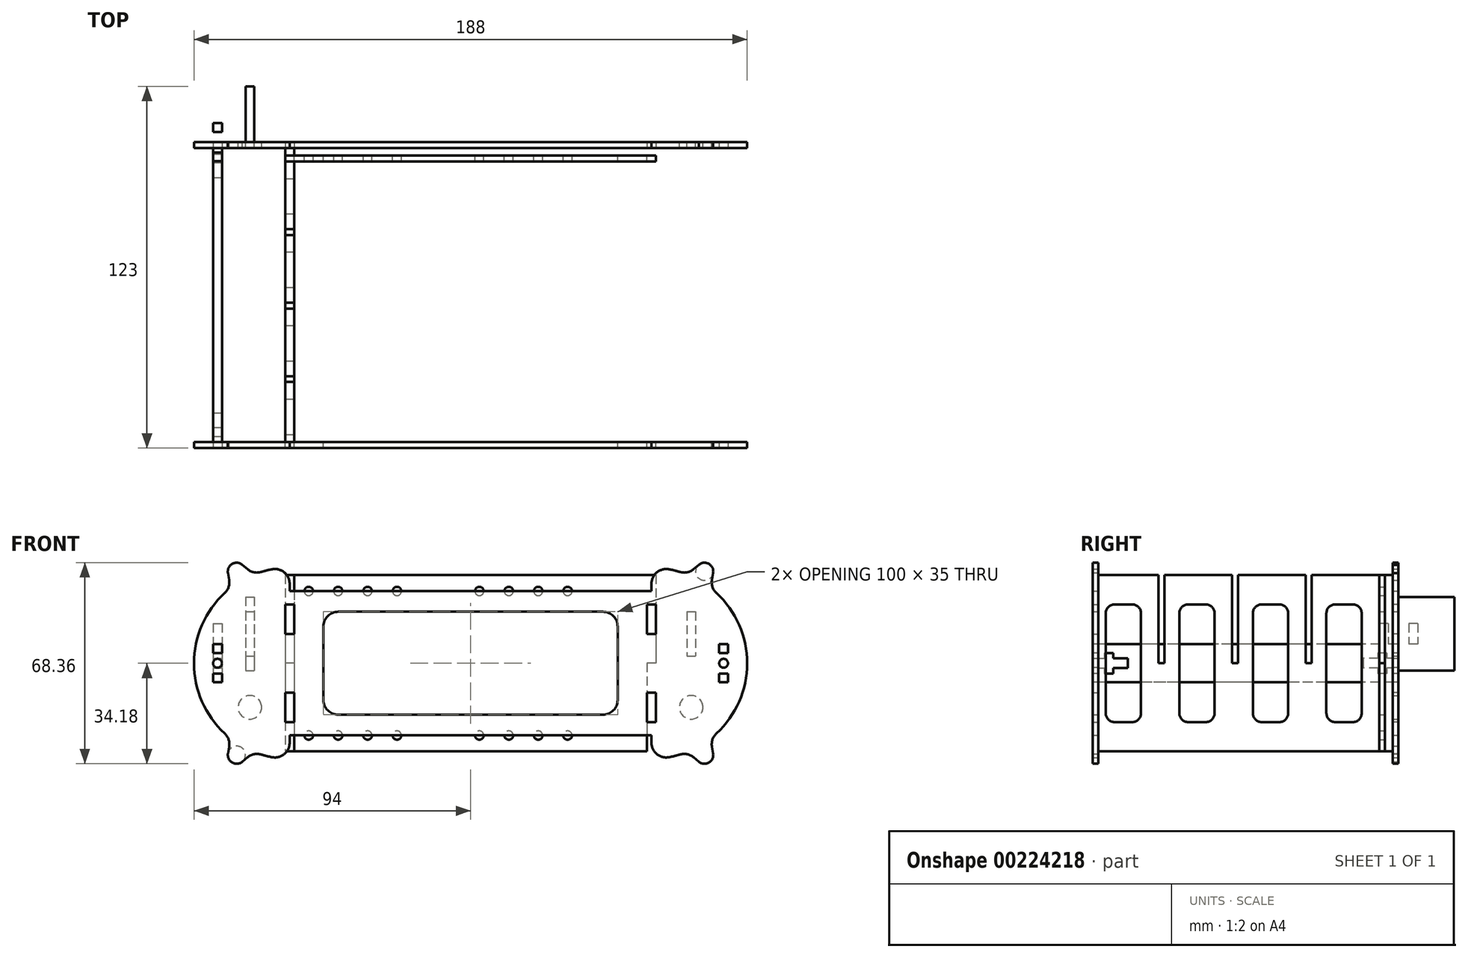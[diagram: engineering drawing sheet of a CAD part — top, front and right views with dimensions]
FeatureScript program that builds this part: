
annotation { "Feature Type Name" : "Feature", "Feature Type Description" : "" }
export const myFeature = defineFeature(function(context is Context, id is Id, definition is map)
    precondition{}
    {
        {
            var Q0;
            Q0=qCreatedBy(makeId("Front.planeOp"),FACE);
            var sketch = newSketch(context, id + "F0", { "sketchPlane" : qUnion([Q0])});
            skLineSegment(sketch, "E0.bottom", {"start": v(-61.5, 42.5) * mm, "end": v(61.5, 42.5) * mm, "construction": true});
            skLineSegment(sketch, "E0.top", {"start": v(-61.5, -42.5) * mm, "end": v(61.5, -42.5) * mm, "construction": true});
            skPoint(sketch, "E0.middle", {"position": v(0, 0) * mm});
            skArc(sketch, "E1", {"start": v(-61.5, 42.5) * mm, "mid": v(-104, 0) * mm, "end": v(-61.5, -42.5) * mm, "construction": true});
            skArc(sketch, "E2", {"start": v(61.5, -42.5) * mm, "mid": v(104, 0) * mm, "end": v(61.5, 42.5) * mm, "construction": true});
            skLineSegment(sketch, "E3.0", {"start": v(-61.5, 39.5) * mm, "end": v(61.5, 39.5) * mm, "construction": true});
            skArc(sketch, "E3.1", {"start": v(-61.5, 39.5) * mm, "mid": v(-101, 0) * mm, "end": v(-61.5, -39.5) * mm, "construction": true});
            skLineSegment(sketch, "E3.2", {"start": v(-61.5, -39.5) * mm, "end": v(61.5, -39.5) * mm, "construction": true});
            skArc(sketch, "E3.3", {"start": v(61.5, -39.5) * mm, "mid": v(101, 0) * mm, "end": v(61.5, 39.5) * mm, "construction": true});
            skArc(sketch, "E4.0", {"start": v(-61.5, 32.5) * mm, "mid": v(-94, 0) * mm, "end": v(-61.5, -32.5) * mm});
            skLineSegment(sketch, "E4.1", {"start": v(-61.5, 32.5) * mm, "end": v(61.5, 32.5) * mm});
            skArc(sketch, "E4.2", {"start": v(61.5, -32.5) * mm, "mid": v(94, 0) * mm, "end": v(61.5, 32.5) * mm});
            skLineSegment(sketch, "E4.3", {"start": v(-61.5, -32.5) * mm, "end": v(61.5, -32.5) * mm});
            skCircle(sketch, "E5", {"center": v(-79.5, 31.18) * mm, "radius": 3 * mm});
            skLineSegment(sketch, "E6", {"start": v(-79.5, 31.18) * mm, "end": v(-61.5, 0) * mm, "construction": true});
            skLineSegment(sketch, "E7", {"start": v(-61.5, 0) * mm, "end": v(-61.5, 32.5) * mm, "construction": true});
            skLineSegment(sketch, "E8", {"start": v(-82.45, 30.66) * mm, "end": v(-81.56, 25.57) * mm});
            skLineSegment(sketch, "E9", {"start": v(-77.57, 33.48) * mm, "end": v(-73.62, 30.16) * mm});
            skLineSegment(sketch, "E10", {"start": v(0, 28.55) * mm, "end": v(0, 0) * mm, "construction": true});
            skLineSegment(sketch, "E11", {"start": v(0, 0) * mm, "end": v(27.55, 0) * mm, "construction": true});
            skCircle(sketch, "E12.MirrorC", {"center": v(79.5, 31.18) * mm, "radius": 3 * mm});
            skLineSegment(sketch, "E13.MirrorCS", {"start": v(77.57, 33.48) * mm, "end": v(73.62, 30.16) * mm});
            skLineSegment(sketch, "E14.MirrorCS", {"start": v(82.45, 30.66) * mm, "end": v(81.56, 25.57) * mm});
            skLineSegment(sketch, "E15.MirrorCS", {"start": v(82.45, -30.66) * mm, "end": v(81.56, -25.57) * mm});
            skCircle(sketch, "E16.MirrorC", {"center": v(79.5, -31.18) * mm, "radius": 3 * mm});
            skLineSegment(sketch, "E17.MirrorCS", {"start": v(77.57, -33.48) * mm, "end": v(73.62, -30.16) * mm});
            skLineSegment(sketch, "E18.MirrorCS", {"start": v(-82.45, -30.66) * mm, "end": v(-81.56, -25.57) * mm});
            skCircle(sketch, "E19.MirrorC", {"center": v(-79.5, -31.18) * mm, "radius": 3 * mm});
            skLineSegment(sketch, "E20.MirrorCS", {"start": v(-77.57, -33.48) * mm, "end": v(-73.62, -30.16) * mm});
            skCircle(sketch, "E21", {"center": v(-75, -15) * mm, "radius": 4 * mm});
            skCircle(sketch, "E22.MirrorC", {"center": v(75, -15) * mm, "radius": 4 * mm});
            skLineSegment(sketch, "E23", {"start": v(-61.5, 32.5) * mm, "end": v(-61.5, 24.5) * mm});
            skLineSegment(sketch, "E24", {"start": v(-61.5, 24.5) * mm, "end": v(61.5, 24.5) * mm});
            skLineSegment(sketch, "E25", {"start": v(61.5, 24.5) * mm, "end": v(61.5, 32.5) * mm});
            skLineSegment(sketch, "E26.MirrorCS", {"start": v(61.5, -24.5) * mm, "end": v(61.5, -32.5) * mm});
            skLineSegment(sketch, "E27.MirrorCS", {"start": v(-61.5, -24.5) * mm, "end": v(61.5, -24.5) * mm});
            skLineSegment(sketch, "E28.MirrorCS", {"start": v(-61.5, 0) * mm, "end": v(-61.5, -32.5) * mm, "construction": true});
            skLineSegment(sketch, "E29", {"start": v(-61.5, -24.5) * mm, "end": v(-61.5, -32.5) * mm});
            skLineSegment(sketch, "E30.bottom", {"start": v(-73.5, 17.5) * mm, "end": v(-76.5, 17.5) * mm});
            skLineSegment(sketch, "E30.top", {"start": v(-73.5, 2.5) * mm, "end": v(-76.5, 2.5) * mm});
            skLineSegment(sketch, "E30.left", {"start": v(-73.5, 17.5) * mm, "end": v(-73.5, 2.5) * mm});
            skLineSegment(sketch, "E30.right", {"start": v(-76.5, 17.5) * mm, "end": v(-76.5, 2.5) * mm});
            skPoint(sketch, "E30.middle", {"position": v(-75, 10) * mm});
            skLineSegment(sketch, "E31.MirrorCS", {"start": v(73.5, 17.5) * mm, "end": v(73.5, 2.5) * mm});
            skLineSegment(sketch, "E32.MirrorCS", {"start": v(73.5, 17.5) * mm, "end": v(76.5, 17.5) * mm});
            skLineSegment(sketch, "E33.MirrorCS", {"start": v(76.5, 17.5) * mm, "end": v(76.5, 2.5) * mm});
            skLineSegment(sketch, "E34.MirrorCS", {"start": v(73.5, 2.5) * mm, "end": v(76.5, 2.5) * mm});
            skSolve(sketch);
        }
        {
            var Q0;
            {var subQ0=sQuery(id+"F0.wireOp",EDGE,"E5");var subQ1=makeQuery(id+"F0.imprint","INTERSECT",VERTEX,{"derivedFrom":[subQ0,sQuery(id+"F0.wireOp",EDGE,"E8")]});Q0=makeQuery(id+"F0.imprint","IMPRINT",FACE,{"disambiguationData":[TD([[makeQuery(id+"F0.imprint","IMPRINT",EDGE,{"disambiguationData":[TD([[subQ1,1.0]])],"derivedFrom":subQ0}),1.0]])]});}
            var Q1;
            {var subQ0=sQuery(id+"F0.wireOp",EDGE,"E12.MirrorC");var subQ1=makeQuery(id+"F0.imprint","INTERSECT",VERTEX,{"derivedFrom":[subQ0,sQuery(id+"F0.wireOp",EDGE,"E13.MirrorCS")]});Q1=makeQuery(id+"F0.imprint","IMPRINT",FACE,{"disambiguationData":[TD([[makeQuery(id+"F0.imprint","IMPRINT",EDGE,{"disambiguationData":[TD([[subQ1,-1.0]])],"derivedFrom":subQ0}),-1.0]])]});}
            var Q2;
            {var subQ0=sQuery(id+"F0.wireOp",EDGE,"E16.MirrorC");var subQ1=makeQuery(id+"F0.imprint","INTERSECT",VERTEX,{"derivedFrom":[sQuery(id+"F0.wireOp",EDGE,"E15.MirrorCS"),subQ0]});Q2=makeQuery(id+"F0.imprint","IMPRINT",FACE,{"disambiguationData":[TD([[makeQuery(id+"F0.imprint","IMPRINT",EDGE,{"disambiguationData":[TD([[subQ1,1.0]])],"derivedFrom":subQ0}),1.0]])]});}
            var Q3;
            {var subQ0=sQuery(id+"F0.wireOp",EDGE,"E19.MirrorC");var subQ1=makeQuery(id+"F0.imprint","INTERSECT",VERTEX,{"derivedFrom":[sQuery(id+"F0.wireOp",EDGE,"E18.MirrorCS"),subQ0]});Q3=makeQuery(id+"F0.imprint","IMPRINT",FACE,{"disambiguationData":[TD([[makeQuery(id+"F0.imprint","IMPRINT",EDGE,{"disambiguationData":[TD([[subQ1,1.0]])],"derivedFrom":subQ0}),-1.0]])]});}
            var Q4;
            {var subQ0=sQuery(id+"F0.wireOp",EDGE,"E8");Q4=makeQuery(id+"F0.imprint","IMPRINT",FACE,{"disambiguationData":[TD([[makeQuery(id+"F0.imprint","IMPRINT",EDGE,{"derivedFrom":subQ0}),1.0]])]});}
            var Q5;
            {var subQ0=sQuery(id+"F0.wireOp",EDGE,"E18.MirrorCS");Q5=makeQuery(id+"F0.imprint","IMPRINT",FACE,{"disambiguationData":[TD([[makeQuery(id+"F0.imprint","IMPRINT",EDGE,{"derivedFrom":subQ0}),-1.0]])]});}
            var Q6;
            {var subQ0=sQuery(id+"F0.wireOp",EDGE,"E15.MirrorCS");Q6=makeQuery(id+"F0.imprint","IMPRINT",FACE,{"disambiguationData":[TD([[makeQuery(id+"F0.imprint","IMPRINT",EDGE,{"derivedFrom":subQ0}),1.0]])]});}
            var Q7;
            {var subQ0=sQuery(id+"F0.wireOp",EDGE,"E13.MirrorCS");Q7=makeQuery(id+"F0.imprint","IMPRINT",FACE,{"disambiguationData":[TD([[makeQuery(id+"F0.imprint","IMPRINT",EDGE,{"derivedFrom":subQ0}),1.0]])]});}
            var Q8;
            Q8=makeQuery(id+"F0.imprint","IMPRINT",FACE,{"disambiguationData":[TD([[makeQuery(id+"F0.imprint","IMPRINT",EDGE,{"derivedFrom":sQuery(id+"F0.wireOp",EDGE,"E21")}),-1.0]])]});
            extrude(context, id + "F1", {"entities" : qUnion([Q0, Q1, Q2, Q3, Q4, Q5, Q6, Q7, Q8]), "depth" : 2 * mm});
        }
        {
            var Q0;
            Q0=makeQuery(id+"F1.opExtrude","SWEPT_EDGE",EDGE,{"disambiguationData":[OSD([sQuery(id+"F0.wireOp",EDGE,"E4.0"),sQuery(id+"F0.wireOp",EDGE,"E9")])]});
            var Q1;
            Q1=makeQuery(id+"F1.opExtrude","SWEPT_EDGE",EDGE,{"disambiguationData":[OSD([sQuery(id+"F0.wireOp",EDGE,"E4.0"),sQuery(id+"F0.wireOp",EDGE,"E8")])]});
            var Q2;
            Q2=makeQuery(id+"F1.opExtrude","SWEPT_EDGE",EDGE,{"disambiguationData":[OSD([sQuery(id+"F0.wireOp",EDGE,"E4.0"),sQuery(id+"F0.wireOp",EDGE,"E4.1"),sQuery(id+"F0.wireOp",EDGE,"E23")])]});
            var Q3;
            Q3=makeQuery(id+"F1.opExtrude","SWEPT_EDGE",EDGE,{"disambiguationData":[OSD([sQuery(id+"F0.wireOp",EDGE,"E4.1"),sQuery(id+"F0.wireOp",EDGE,"E4.2"),sQuery(id+"F0.wireOp",EDGE,"E25")])]});
            var Q4;
            Q4=makeQuery(id+"F1.opExtrude","SWEPT_EDGE",EDGE,{"disambiguationData":[OSD([sQuery(id+"F0.wireOp",EDGE,"E4.2"),sQuery(id+"F0.wireOp",EDGE,"E13.MirrorCS")])]});
            var Q5;
            Q5=makeQuery(id+"F1.opExtrude","SWEPT_EDGE",EDGE,{"disambiguationData":[OSD([sQuery(id+"F0.wireOp",EDGE,"E4.2"),sQuery(id+"F0.wireOp",EDGE,"E14.MirrorCS")])]});
            var Q6;
            Q6=makeQuery(id+"F1.opExtrude","SWEPT_EDGE",EDGE,{"disambiguationData":[OSD([sQuery(id+"F0.wireOp",EDGE,"E4.2"),sQuery(id+"F0.wireOp",EDGE,"E15.MirrorCS")])]});
            var Q7;
            Q7=makeQuery(id+"F1.opExtrude","SWEPT_EDGE",EDGE,{"disambiguationData":[OSD([sQuery(id+"F0.wireOp",EDGE,"E4.2"),sQuery(id+"F0.wireOp",EDGE,"E17.MirrorCS")])]});
            var Q8;
            Q8=makeQuery(id+"F1.opExtrude","SWEPT_EDGE",EDGE,{"disambiguationData":[OSD([sQuery(id+"F0.wireOp",EDGE,"E4.2"),sQuery(id+"F0.wireOp",EDGE,"E4.3"),sQuery(id+"F0.wireOp",EDGE,"E26.MirrorCS")])]});
            var Q9;
            Q9=makeQuery(id+"F1.opExtrude","SWEPT_EDGE",EDGE,{"disambiguationData":[OSD([sQuery(id+"F0.wireOp",EDGE,"E4.0"),sQuery(id+"F0.wireOp",EDGE,"E4.3"),sQuery(id+"F0.wireOp",EDGE,"E29")])]});
            var Q10;
            Q10=makeQuery(id+"F1.opExtrude","SWEPT_EDGE",EDGE,{"disambiguationData":[OSD([sQuery(id+"F0.wireOp",EDGE,"E4.0"),sQuery(id+"F0.wireOp",EDGE,"E20.MirrorCS")])]});
            var Q11;
            Q11=makeQuery(id+"F1.opExtrude","SWEPT_EDGE",EDGE,{"disambiguationData":[OSD([sQuery(id+"F0.wireOp",EDGE,"E4.0"),sQuery(id+"F0.wireOp",EDGE,"E18.MirrorCS")])]});
            fillet(context, id + "F2", {"entities" : qUnion([Q0, Q1, Q2, Q3, Q4, Q5, Q6, Q7, Q8, Q9, Q10, Q11]), "radius" : 5 * mm, "tangentPropagation" : true, "allowEdgeOverflow" : false});
        }
        {
            var Q0;
            Q0=makeQuery(id+"F1.opExtrude","SWEPT_FACE",FACE,{"disambiguationData":[OSD([sQuery(id+"F0.wireOp",EDGE,"E30.left")])]});
            var sketch = newSketch(context, id + "F3", { "sketchPlane" : qUnion([Q0])});
            skPoint(sketch, "E35.0", {"position": v(2, 17.5) * mm});
            skPoint(sketch, "E35.1", {"position": v(0, 2.5) * mm});
            skLineSegment(sketch, "E36.bottom", {"start": v(2, 17.5) * mm, "end": v(0, 17.5) * mm});
            skLineSegment(sketch, "E36.top", {"start": v(2, 2.5) * mm, "end": v(0, 2.5) * mm});
            skLineSegment(sketch, "E36.left", {"start": v(2, 17.5) * mm, "end": v(2, 2.5) * mm});
            skLineSegment(sketch, "E36.right", {"start": v(0, 17.5) * mm, "end": v(0, 2.5) * mm});
            skLineSegment(sketch, "E37.bottom", {"start": v(0, 22.5) * mm, "end": v(-19, 22.5) * mm});
            skLineSegment(sketch, "E37.top", {"start": v(0, -2.5) * mm, "end": v(-19, -2.5) * mm});
            skLineSegment(sketch, "E37.left", {"start": v(0, 22.5) * mm, "end": v(0, -2.5) * mm});
            skLineSegment(sketch, "E37.right", {"start": v(-19, 22.5) * mm, "end": v(-19, -2.5) * mm});
            skPoint(sketch, "E38", {"position": v(0, 10) * mm});
            skSolve(sketch);
        }
        {
            var Q0;
            Q0 = qSketchRegion(id + "F3", true);
            extrude(context, id + "F4", {"entities" : qUnion([Q0]), "depth" : 3 * mm});
        }
        {
            var Q0;
            Q0=makeQuery(id+"F1.opExtrude","CAP_FACE",FACE,{"disambiguationData":[OSD([sQuery(id+"F0.wireOp",EDGE,"E4.0"),sQuery(id+"F0.wireOp",EDGE,"E4.2"),sQuery(id+"F0.wireOp",EDGE,"E5"),sQuery(id+"F0.wireOp",EDGE,"E8"),sQuery(id+"F0.wireOp",EDGE,"E9"),sQuery(id+"F0.wireOp",EDGE,"E12.MirrorC"),sQuery(id+"F0.wireOp",EDGE,"E13.MirrorCS"),sQuery(id+"F0.wireOp",EDGE,"E14.MirrorCS"),sQuery(id+"F0.wireOp",EDGE,"E15.MirrorCS"),sQuery(id+"F0.wireOp",EDGE,"E16.MirrorC"),sQuery(id+"F0.wireOp",EDGE,"E17.MirrorCS"),sQuery(id+"F0.wireOp",EDGE,"E18.MirrorCS"),sQuery(id+"F0.wireOp",EDGE,"E19.MirrorC"),sQuery(id+"F0.wireOp",EDGE,"E20.MirrorCS"),sQuery(id+"F0.wireOp",EDGE,"E21"),sQuery(id+"F0.wireOp",EDGE,"E22.MirrorC"),sQuery(id+"F0.wireOp",EDGE,"E23"),sQuery(id+"F0.wireOp",EDGE,"E24"),sQuery(id+"F0.wireOp",EDGE,"E25"),sQuery(id+"F0.wireOp",EDGE,"E26.MirrorCS"),sQuery(id+"F0.wireOp",EDGE,"E27.MirrorCS"),sQuery(id+"F0.wireOp",EDGE,"E29"),sQuery(id+"F0.wireOp",EDGE,"E30.bottom"),sQuery(id+"F0.wireOp",EDGE,"E30.top"),sQuery(id+"F0.wireOp",EDGE,"E30.left"),sQuery(id+"F0.wireOp",EDGE,"E30.right"),sQuery(id+"F0.wireOp",EDGE,"E31.MirrorCS"),sQuery(id+"F0.wireOp",EDGE,"E32.MirrorCS"),sQuery(id+"F0.wireOp",EDGE,"E33.MirrorCS"),sQuery(id+"F0.wireOp",EDGE,"E34.MirrorCS")])],"isStart":false});
            var sketch = newSketch(context, id + "F5", { "sketchPlane" : qUnion([Q0])});
            skLineSegment(sketch, "E39.bottom", {"start": v(60, 20) * mm, "end": v(63, 20) * mm});
            skLineSegment(sketch, "E39.top", {"start": v(60, 10) * mm, "end": v(63, 10) * mm});
            skLineSegment(sketch, "E39.left", {"start": v(60, 20) * mm, "end": v(60, 10) * mm});
            skLineSegment(sketch, "E39.right", {"start": v(63, 20) * mm, "end": v(63, 10) * mm});
            skLineSegment(sketch, "E40", {"start": v(0, 0) * mm, "end": v(0, 17.53) * mm, "construction": true});
            skLineSegment(sketch, "E41", {"start": v(0, 0) * mm, "end": v(16.07, 0) * mm, "construction": true});
            skLineSegment(sketch, "E42.MirrorCS", {"start": v(60, -20) * mm, "end": v(63, -20) * mm});
            skLineSegment(sketch, "E43.MirrorCS", {"start": v(60, -10) * mm, "end": v(63, -10) * mm});
            skLineSegment(sketch, "E44.MirrorCS", {"start": v(60, -20) * mm, "end": v(60, -10) * mm});
            skLineSegment(sketch, "E45.MirrorCS", {"start": v(63, -20) * mm, "end": v(63, -10) * mm});
            skLineSegment(sketch, "E46.MirrorCS", {"start": v(-60, 10) * mm, "end": v(-63, 10) * mm});
            skLineSegment(sketch, "E47.MirrorCS", {"start": v(-60, 20) * mm, "end": v(-60, 10) * mm});
            skLineSegment(sketch, "E48.MirrorCS", {"start": v(-63, 20) * mm, "end": v(-63, 10) * mm});
            skLineSegment(sketch, "E49.MirrorCS", {"start": v(-60, 20) * mm, "end": v(-63, 20) * mm});
            skLineSegment(sketch, "E50.MirrorCS", {"start": v(-60, -20) * mm, "end": v(-60, -10) * mm});
            skLineSegment(sketch, "E51.MirrorCS", {"start": v(-60, -20) * mm, "end": v(-63, -20) * mm});
            skLineSegment(sketch, "E52.MirrorCS", {"start": v(-63, -20) * mm, "end": v(-63, -10) * mm});
            skLineSegment(sketch, "E53.MirrorCS", {"start": v(-60, -10) * mm, "end": v(-63, -10) * mm});
            skSolve(sketch);
        }
        {
            var Q0;
            Q0 = qSketchRegion(id + "F5", true);
            extrude(context, id + "F6", {"entities" : qUnion([Q0]), "operationType" : NewBodyOperationType.REMOVE, "oppositeDirection" : true, "depth" : 25 * mm});
        }
        {
            var Q0;
            Q0=makeQuery(id+"F6.boolean.opBoolean","COPY",FACE,{"derivedFrom":makeQuery(id+"F6.opExtrude","SWEPT_FACE",FACE,{"disambiguationData":[OSD([sQuery(id+"F5.wireOp",EDGE,"E48.MirrorCS")])]})});
            var sketch = newSketch(context, id + "F7", { "sketchPlane" : qUnion([Q0])});
            skLineSegment(sketch, "E54.bottom", {"start": v(-2, 30) * mm, "end": v(-102, 30) * mm});
            skLineSegment(sketch, "E54.top", {"start": v(-2, -30) * mm, "end": v(-102, -30) * mm});
            skLineSegment(sketch, "E54.left", {"start": v(-2, 30) * mm, "end": v(-2, -30) * mm});
            skLineSegment(sketch, "E54.right", {"start": v(-102, 30) * mm, "end": v(-102, -30) * mm});
            skPoint(sketch, "E54.middle", {"position": v(-52, 0) * mm});
            skLineSegment(sketch, "E55.0.0", {"start": v(0, 20) * mm, "end": v(-2, 20) * mm});
            skLineSegment(sketch, "E55.0.1", {"start": v(-2, 20) * mm, "end": v(-2, 10) * mm});
            skLineSegment(sketch, "E55.0.2", {"start": v(-2, 10) * mm, "end": v(0, 10) * mm});
            skLineSegment(sketch, "E55.0.3", {"start": v(0, 10) * mm, "end": v(0, 20) * mm});
            skLineSegment(sketch, "E55.1.0", {"start": v(0, -20) * mm, "end": v(0, -10) * mm});
            skLineSegment(sketch, "E55.1.1", {"start": v(0, -10) * mm, "end": v(-2, -10) * mm});
            skLineSegment(sketch, "E55.1.2", {"start": v(-2, -10) * mm, "end": v(-2, -20) * mm});
            skLineSegment(sketch, "E55.1.3", {"start": v(-2, -20) * mm, "end": v(0, -20) * mm});
            skLineSegment(sketch, "E56", {"start": v(-52, 30) * mm, "end": v(-52, -30) * mm, "construction": true});
            skLineSegment(sketch, "E57.MirrorCS", {"start": v(-104, 20) * mm, "end": v(-102, 20) * mm});
            skLineSegment(sketch, "E58.MirrorCS", {"start": v(-104, 10) * mm, "end": v(-104, 20) * mm});
            skLineSegment(sketch, "E59.MirrorCS", {"start": v(-102, 10) * mm, "end": v(-104, 10) * mm});
            skLineSegment(sketch, "E60.MirrorCS", {"start": v(-104, -10) * mm, "end": v(-102, -10) * mm});
            skLineSegment(sketch, "E61.MirrorCS", {"start": v(-104, -20) * mm, "end": v(-104, -10) * mm});
            skLineSegment(sketch, "E62.MirrorCS", {"start": v(-102, -20) * mm, "end": v(-104, -20) * mm});
            skLineSegment(sketch, "E63.bottom", {"start": v(-4.58, 30) * mm, "end": v(-6.58, 30) * mm});
            skLineSegment(sketch, "E63.top", {"start": v(-4.58, 0) * mm, "end": v(-6.58, 0) * mm});
            skLineSegment(sketch, "E63.left", {"start": v(-4.58, 30) * mm, "end": v(-4.58, 0) * mm});
            skLineSegment(sketch, "E63.right", {"start": v(-6.58, 30) * mm, "end": v(-6.58, 0) * mm});
            skPoint(sketch, "E63.middle", {"position": v(-5.58, 15) * mm});
            skLineSegment(sketch, "E64", {"start": v(-52, 0) * mm, "end": v(-39.54, 0) * mm, "construction": true});
            skLineSegment(sketch, "E65.bottom", {"start": v(-15.5, 20) * mm, "end": v(-21.5, 20) * mm});
            skLineSegment(sketch, "E65.top", {"start": v(-15.5, -20) * mm, "end": v(-21.5, -20) * mm});
            skLineSegment(sketch, "E65.left", {"start": v(-12.5, 17) * mm, "end": v(-12.5, -17) * mm});
            skLineSegment(sketch, "E65.right", {"start": v(-24.5, 17) * mm, "end": v(-24.5, -17) * mm});
            skPoint(sketch, "E65.middle", {"position": v(-18.5, 0) * mm});
            skPoint(sketch, "E66", {"position": v(-18.5, 18.1) * mm});
            skPoint(sketch, "E67.visualSharp", {"position": v(-24.5, 20) * mm});
            skArc(sketch, "E67.filletArc", {"start": v(-21.5, 20) * mm, "mid": v(-23.62, 19.12) * mm, "end": v(-24.5, 17) * mm});
            skPoint(sketch, "E68.visualSharp", {"position": v(-12.5, 20) * mm});
            skArc(sketch, "E68.filletArc", {"start": v(-12.5, 17) * mm, "mid": v(-13.38, 19.12) * mm, "end": v(-15.5, 20) * mm});
            skPoint(sketch, "E69.visualSharp", {"position": v(-12.5, -20) * mm});
            skArc(sketch, "E69.filletArc", {"start": v(-15.5, -20) * mm, "mid": v(-13.38, -19.12) * mm, "end": v(-12.5, -17) * mm});
            skPoint(sketch, "E70.visualSharp", {"position": v(-24.5, -20) * mm});
            skArc(sketch, "E70.filletArc", {"start": v(-24.5, -17) * mm, "mid": v(-23.62, -19.12) * mm, "end": v(-21.5, -20) * mm});
            skLineSegment(sketch, "E71.1.0.0", {"start": v(-40.5, 20) * mm, "end": v(-46.5, 20) * mm});
            skArc(sketch, "E71.1.0.1", {"start": v(-46.5, 20) * mm, "mid": v(-48.62, 19.12) * mm, "end": v(-49.5, 17) * mm});
            skArc(sketch, "E71.1.0.2", {"start": v(-37.5, 17) * mm, "mid": v(-38.38, 19.12) * mm, "end": v(-40.5, 20) * mm});
            skLineSegment(sketch, "E71.1.0.3", {"start": v(-37.5, 17) * mm, "end": v(-37.5, -17) * mm});
            skArc(sketch, "E71.1.0.4", {"start": v(-40.5, -20) * mm, "mid": v(-38.38, -19.12) * mm, "end": v(-37.5, -17) * mm});
            skLineSegment(sketch, "E71.1.0.5", {"start": v(-40.5, -20) * mm, "end": v(-46.5, -20) * mm});
            skArc(sketch, "E71.1.0.6", {"start": v(-49.5, -17) * mm, "mid": v(-48.62, -19.12) * mm, "end": v(-46.5, -20) * mm});
            skLineSegment(sketch, "E71.1.0.7", {"start": v(-49.5, 17) * mm, "end": v(-49.5, -17) * mm});
            skLineSegment(sketch, "E71.2.0.0", {"start": v(-65.5, 20) * mm, "end": v(-71.5, 20) * mm});
            skArc(sketch, "E71.2.0.1", {"start": v(-71.5, 20) * mm, "mid": v(-73.62, 19.12) * mm, "end": v(-74.5, 17) * mm});
            skArc(sketch, "E71.2.0.2", {"start": v(-62.5, 17) * mm, "mid": v(-63.38, 19.12) * mm, "end": v(-65.5, 20) * mm});
            skLineSegment(sketch, "E71.2.0.3", {"start": v(-62.5, 17) * mm, "end": v(-62.5, -17) * mm});
            skArc(sketch, "E71.2.0.4", {"start": v(-65.5, -20) * mm, "mid": v(-63.38, -19.12) * mm, "end": v(-62.5, -17) * mm});
            skLineSegment(sketch, "E71.2.0.5", {"start": v(-65.5, -20) * mm, "end": v(-71.5, -20) * mm});
            skArc(sketch, "E71.2.0.6", {"start": v(-74.5, -17) * mm, "mid": v(-73.62, -19.12) * mm, "end": v(-71.5, -20) * mm});
            skLineSegment(sketch, "E71.2.0.7", {"start": v(-74.5, 17) * mm, "end": v(-74.5, -17) * mm});
            skLineSegment(sketch, "E71.direction1", {"start": v(-21.5, 20) * mm, "end": v(-46.5, 20) * mm, "construction": true});
            skLineSegment(sketch, "E72.0.3.0", {"start": v(-90.5, 20) * mm, "end": v(-96.5, 20) * mm});
            skArc(sketch, "E72.3.3.0", {"start": v(-96.5, 20) * mm, "mid": v(-98.62, 19.12) * mm, "end": v(-99.5, 17) * mm});
            skArc(sketch, "E72.7.3.0", {"start": v(-87.5, 17) * mm, "mid": v(-88.38, 19.12) * mm, "end": v(-90.5, 20) * mm});
            skLineSegment(sketch, "E72.11.3.0", {"start": v(-87.5, 17) * mm, "end": v(-87.5, -17) * mm});
            skArc(sketch, "E72.14.3.0", {"start": v(-90.5, -20) * mm, "mid": v(-88.38, -19.12) * mm, "end": v(-87.5, -17) * mm});
            skLineSegment(sketch, "E72.18.3.0", {"start": v(-90.5, -20) * mm, "end": v(-96.5, -20) * mm});
            skArc(sketch, "E72.21.3.0", {"start": v(-99.5, -17) * mm, "mid": v(-98.62, -19.12) * mm, "end": v(-96.5, -20) * mm});
            skLineSegment(sketch, "E72.25.3.0", {"start": v(-99.5, 17) * mm, "end": v(-99.5, -17) * mm});
            skLineSegment(sketch, "E73.0.1.0", {"start": v(-31.58, 30) * mm, "end": v(-31.58, 0) * mm});
            skLineSegment(sketch, "E73.3.1.0", {"start": v(-29.58, 30) * mm, "end": v(-31.58, 30) * mm});
            skLineSegment(sketch, "E73.6.1.0", {"start": v(-29.58, 30) * mm, "end": v(-29.58, 0) * mm});
            skLineSegment(sketch, "E73.9.1.0", {"start": v(-29.58, 0) * mm, "end": v(-31.58, 0) * mm});
            skLineSegment(sketch, "E73.0.2.0", {"start": v(-56.58, 30) * mm, "end": v(-56.58, 0) * mm});
            skLineSegment(sketch, "E73.3.2.0", {"start": v(-54.58, 30) * mm, "end": v(-56.58, 30) * mm});
            skLineSegment(sketch, "E73.6.2.0", {"start": v(-54.58, 30) * mm, "end": v(-54.58, 0) * mm});
            skLineSegment(sketch, "E73.9.2.0", {"start": v(-54.58, 0) * mm, "end": v(-56.58, 0) * mm});
            skLineSegment(sketch, "E73.0.3.0", {"start": v(-81.58, 30) * mm, "end": v(-81.58, 0) * mm});
            skLineSegment(sketch, "E73.3.3.0", {"start": v(-79.58, 30) * mm, "end": v(-81.58, 30) * mm});
            skLineSegment(sketch, "E73.6.3.0", {"start": v(-79.58, 30) * mm, "end": v(-79.58, 0) * mm});
            skLineSegment(sketch, "E73.9.3.0", {"start": v(-79.58, 0) * mm, "end": v(-81.58, 0) * mm});
            skSolve(sketch);
        }
        {
            var Q0;
            {var subQ9=sQuery(id+"F7.wireOp",EDGE,"E54.top");Q0=makeQuery(id+"F7.imprint","IMPRINT",FACE,{"disambiguationData":[TD([[makeQuery(id+"F7.imprint","IMPRINT",EDGE,{"derivedFrom":subQ9}),-1.0]])]});}
            var Q1;
            {var subQ0=sQuery(id+"F7.wireOp",EDGE,"E57.MirrorCS");Q1=makeQuery(id+"F7.imprint","IMPRINT",FACE,{"disambiguationData":[TD([[makeQuery(id+"F7.imprint","IMPRINT",EDGE,{"derivedFrom":subQ0}),-1.0]])]});}
            var Q2;
            {var subQ0=sQuery(id+"F7.wireOp",EDGE,"E60.MirrorCS");Q2=makeQuery(id+"F7.imprint","IMPRINT",FACE,{"disambiguationData":[TD([[makeQuery(id+"F7.imprint","IMPRINT",EDGE,{"derivedFrom":subQ0}),-1.0]])]});}
            var Q3;
            Q3=makeQuery(id+"F7.imprint","IMPRINT",FACE,{"disambiguationData":[TD([[makeQuery(id+"F7.imprint","IMPRINT",EDGE,{"derivedFrom":sQuery(id+"F7.wireOp",EDGE,"E55.0.0")}),1.0]])]});
            var Q4;
            Q4=makeQuery(id+"F7.imprint","IMPRINT",FACE,{"disambiguationData":[TD([[makeQuery(id+"F7.imprint","IMPRINT",EDGE,{"derivedFrom":sQuery(id+"F7.wireOp",EDGE,"E55.1.0")}),1.0]])]});
            extrude(context, id + "F8", {"entities" : qUnion([Q0, Q1, Q2, Q3, Q4]), "depth" : 3 * mm});
        }
        {
            var Q0;
            Q0=makeQuery(id+"F8.opExtrude","SWEPT_FACE",FACE,{"disambiguationData":[OSD([sQuery(id+"F7.wireOp",EDGE,"E63.left")])]});
            var sketch = newSketch(context, id + "F9", { "sketchPlane" : qUnion([Q0])});
            skLineSegment(sketch, "E74.bottom", {"start": v(-60, 30) * mm, "end": v(60, 30) * mm});
            skLineSegment(sketch, "E74.top", {"start": v(-60, -30) * mm, "end": v(60, -30) * mm});
            skLineSegment(sketch, "E74.left", {"start": v(-60, 30) * mm, "end": v(-60, -30) * mm});
            skLineSegment(sketch, "E74.right", {"start": v(60, 30) * mm, "end": v(60, -30) * mm});
            skPoint(sketch, "E74.middle", {"position": v(0, 0) * mm});
            skLineSegment(sketch, "E75", {"start": v(0, 0) * mm, "end": v(0, 15.93) * mm, "construction": true});
            skCircle(sketch, "E76", {"center": v(-55, 24.5) * mm, "radius": 1.5 * mm});
            skCircle(sketch, "E77", {"center": v(3, 24.5) * mm, "radius": 1.5 * mm});
            skCircle(sketch, "E78", {"center": v(-55, -24.5) * mm, "radius": 1.5 * mm});
            skCircle(sketch, "E79", {"center": v(3, -24.5) * mm, "radius": 1.5 * mm});
            skLineSegment(sketch, "E80", {"start": v(3, 24.5) * mm, "end": v(3, -24.5) * mm, "construction": true});
            skPoint(sketch, "E81", {"position": v(3, 0) * mm});
            skCircle(sketch, "E82.1.0.0", {"center": v(-45, 24.5) * mm, "radius": 1.5 * mm});
            skCircle(sketch, "E82.1.0.1", {"center": v(13, 24.5) * mm, "radius": 1.5 * mm});
            skCircle(sketch, "E82.1.0.2", {"center": v(13, -24.5) * mm, "radius": 1.5 * mm});
            skCircle(sketch, "E82.1.0.3", {"center": v(-45, -24.5) * mm, "radius": 1.5 * mm});
            skCircle(sketch, "E82.2.0.0", {"center": v(-35, 24.5) * mm, "radius": 1.5 * mm});
            skCircle(sketch, "E82.2.0.1", {"center": v(23, 24.5) * mm, "radius": 1.5 * mm});
            skCircle(sketch, "E82.2.0.2", {"center": v(23, -24.5) * mm, "radius": 1.5 * mm});
            skCircle(sketch, "E82.2.0.3", {"center": v(-35, -24.5) * mm, "radius": 1.5 * mm});
            skCircle(sketch, "E82.3.0.0", {"center": v(-25, 24.5) * mm, "radius": 1.5 * mm});
            skCircle(sketch, "E82.3.0.1", {"center": v(33, 24.5) * mm, "radius": 1.5 * mm});
            skCircle(sketch, "E82.3.0.2", {"center": v(33, -24.5) * mm, "radius": 1.5 * mm});
            skCircle(sketch, "E82.3.0.3", {"center": v(-25, -24.5) * mm, "radius": 1.5 * mm});
            skLineSegment(sketch, "E82.direction1", {"start": v(-55, 24.5) * mm, "end": v(-45, 24.5) * mm, "construction": true});
            skLineSegment(sketch, "E83.bottom", {"start": v(-45, 17.5) * mm, "end": v(45, 17.5) * mm});
            skLineSegment(sketch, "E83.top", {"start": v(-45, -17.5) * mm, "end": v(45, -17.5) * mm});
            skLineSegment(sketch, "E83.left", {"start": v(-50, 12.5) * mm, "end": v(-50, -12.5) * mm});
            skLineSegment(sketch, "E83.right", {"start": v(50, 12.5) * mm, "end": v(50, -12.5) * mm});
            skPoint(sketch, "E84.visualSharp", {"position": v(-50, 17.5) * mm});
            skArc(sketch, "E84.filletArc", {"start": v(-45, 17.5) * mm, "mid": v(-48.54, 16.04) * mm, "end": v(-50, 12.5) * mm});
            skPoint(sketch, "E85.visualSharp", {"position": v(-50, -17.5) * mm});
            skArc(sketch, "E85.filletArc", {"start": v(-50, -12.5) * mm, "mid": v(-48.54, -16.04) * mm, "end": v(-45, -17.5) * mm});
            skPoint(sketch, "E86.visualSharp", {"position": v(50, -17.5) * mm});
            skArc(sketch, "E86.filletArc", {"start": v(45, -17.5) * mm, "mid": v(48.54, -16.04) * mm, "end": v(50, -12.5) * mm});
            skPoint(sketch, "E87.visualSharp", {"position": v(50, 17.5) * mm});
            skArc(sketch, "E87.filletArc", {"start": v(50, 12.5) * mm, "mid": v(48.54, 16.04) * mm, "end": v(45, 17.5) * mm});
            skLineSegment(sketch, "E88.0.0", {"start": v(-63, 30) * mm, "end": v(-63, 0) * mm});
            skLineSegment(sketch, "E88.0.1", {"start": v(-63, 0) * mm, "end": v(-60, 0) * mm});
            skLineSegment(sketch, "E88.0.2", {"start": v(-60, 0) * mm, "end": v(-60, 30) * mm});
            skLineSegment(sketch, "E88.0.3", {"start": v(-60, 30) * mm, "end": v(-63, 30) * mm});
            skLineSegment(sketch, "E89.MirrorCS", {"start": v(60, 30) * mm, "end": v(63, 30) * mm});
            skLineSegment(sketch, "E90.MirrorCS", {"start": v(63, 30) * mm, "end": v(63, 0) * mm});
            skLineSegment(sketch, "E91.MirrorCS", {"start": v(63, 0) * mm, "end": v(60, 0) * mm});
            skSolve(sketch);
        }
        {
            var Q0;
            Q0 = qSketchRegion(id + "F9", true);
            extrude(context, id + "F10", {"entities" : qUnion([Q0]), "depth" : 2 * mm});
        }
        {
            var Q0;
            {var subQ0=sQuery(id+"F7.wireOp",EDGE,"E54.right");Q0=makeQuery(id+"F8.opExtrude","SWEPT_FACE",FACE,{"disambiguationData":[OSD([subQ0]),TDD([makeQuery(id+"F7.imprint","IMPRINT",EDGE,{"disambiguationData":[TD([[makeQuery(id+"F7.imprint","INTERSECT",VERTEX,{"derivedFrom":[sQuery(id+"F7.wireOp",EDGE,"E54.bottom"),subQ0]}),-1.0]])],"derivedFrom":subQ0})])]});}
            var sketch = newSketch(context, id + "F11", { "sketchPlane" : qUnion([Q0])});
            skLineSegment(sketch, "E92.0.0", {"start": v(-61.5, 24.5) * mm, "end": v(-61.5, 27.04) * mm});
            skArc(sketch, "E92.0.1", {"start": v(-61.5, 27.04) * mm, "mid": v(-63.3, 30.89) * mm, "end": v(-67.4, 31.96) * mm});
            skArc(sketch, "E92.0.2", {"start": v(-67.4, 31.96) * mm, "mid": v(-69.27, 31.56) * mm, "end": v(-71.11, 31.05) * mm});
            skArc(sketch, "E92.0.3", {"start": v(-71.11, 31.05) * mm, "mid": v(-73.58, 30.92) * mm, "end": v(-75.8, 32) * mm});
            skLineSegment(sketch, "E92.0.4", {"start": v(-75.8, 32) * mm, "end": v(-77.57, 33.48) * mm});
            skArc(sketch, "E92.0.5", {"start": v(-77.57, 33.48) * mm, "mid": v(-81, 33.77) * mm, "end": v(-82.45, 30.66) * mm});
            skLineSegment(sketch, "E92.0.6", {"start": v(-82.45, 30.66) * mm, "end": v(-82.05, 28.38) * mm});
            skArc(sketch, "E92.0.7", {"start": v(-82.05, 28.38) * mm, "mid": v(-82.24, 25.92) * mm, "end": v(-83.58, 23.85) * mm});
            skArc(sketch, "E92.0.8", {"start": v(-83.58, 23.85) * mm, "mid": v(-94, 0) * mm, "end": v(-83.58, -23.85) * mm});
            skArc(sketch, "E92.0.9", {"start": v(-83.58, -23.85) * mm, "mid": v(-82.24, -25.92) * mm, "end": v(-82.05, -28.38) * mm});
            skLineSegment(sketch, "E92.0.10", {"start": v(-82.05, -28.38) * mm, "end": v(-82.45, -30.66) * mm});
            skArc(sketch, "E92.0.11", {"start": v(-82.45, -30.66) * mm, "mid": v(-81, -33.77) * mm, "end": v(-77.57, -33.48) * mm});
            skLineSegment(sketch, "E92.0.12", {"start": v(-77.57, -33.48) * mm, "end": v(-75.8, -32) * mm});
            skArc(sketch, "E92.0.13", {"start": v(-75.8, -32) * mm, "mid": v(-73.58, -30.92) * mm, "end": v(-71.11, -31.05) * mm});
            skArc(sketch, "E92.0.14", {"start": v(-71.11, -31.05) * mm, "mid": v(-69.27, -31.56) * mm, "end": v(-67.4, -31.96) * mm});
            skArc(sketch, "E92.0.15", {"start": v(-67.4, -31.96) * mm, "mid": v(-63.3, -30.89) * mm, "end": v(-61.5, -27.04) * mm});
            skLineSegment(sketch, "E92.0.16", {"start": v(-61.5, -27.04) * mm, "end": v(-61.5, -24.5) * mm});
            skLineSegment(sketch, "E92.0.17", {"start": v(-61.5, -24.5) * mm, "end": v(61.5, -24.5) * mm});
            skLineSegment(sketch, "E92.0.18", {"start": v(61.5, -24.5) * mm, "end": v(61.5, -27.04) * mm});
            skArc(sketch, "E92.0.19", {"start": v(61.5, -27.04) * mm, "mid": v(63.3, -30.89) * mm, "end": v(67.4, -31.96) * mm});
            skArc(sketch, "E92.0.20", {"start": v(67.4, -31.96) * mm, "mid": v(69.27, -31.56) * mm, "end": v(71.11, -31.05) * mm});
            skArc(sketch, "E92.0.21", {"start": v(71.11, -31.05) * mm, "mid": v(73.58, -30.92) * mm, "end": v(75.8, -32) * mm});
            skLineSegment(sketch, "E92.0.22", {"start": v(75.8, -32) * mm, "end": v(77.57, -33.48) * mm});
            skArc(sketch, "E92.0.23", {"start": v(77.57, -33.48) * mm, "mid": v(81, -33.77) * mm, "end": v(82.45, -30.66) * mm});
            skLineSegment(sketch, "E92.0.24", {"start": v(82.45, -30.66) * mm, "end": v(82.05, -28.38) * mm});
            skArc(sketch, "E92.0.25", {"start": v(82.05, -28.38) * mm, "mid": v(82.24, -25.92) * mm, "end": v(83.58, -23.85) * mm});
            skArc(sketch, "E92.0.26", {"start": v(83.58, -23.85) * mm, "mid": v(94, 0) * mm, "end": v(83.58, 23.85) * mm});
            skArc(sketch, "E92.0.27", {"start": v(83.58, 23.85) * mm, "mid": v(82.24, 25.92) * mm, "end": v(82.05, 28.38) * mm});
            skLineSegment(sketch, "E92.0.28", {"start": v(82.05, 28.38) * mm, "end": v(82.45, 30.66) * mm});
            skArc(sketch, "E92.0.29", {"start": v(82.45, 30.66) * mm, "mid": v(81, 33.77) * mm, "end": v(77.57, 33.48) * mm});
            skLineSegment(sketch, "E92.0.30", {"start": v(77.57, 33.48) * mm, "end": v(75.8, 32) * mm});
            skArc(sketch, "E92.0.31", {"start": v(75.8, 32) * mm, "mid": v(73.58, 30.92) * mm, "end": v(71.11, 31.05) * mm});
            skArc(sketch, "E92.0.32", {"start": v(71.11, 31.05) * mm, "mid": v(69.27, 31.56) * mm, "end": v(67.4, 31.96) * mm});
            skArc(sketch, "E92.0.33", {"start": v(67.4, 31.96) * mm, "mid": v(63.3, 30.89) * mm, "end": v(61.5, 27.04) * mm});
            skLineSegment(sketch, "E92.0.34", {"start": v(61.5, 27.04) * mm, "end": v(61.5, 24.5) * mm});
            skLineSegment(sketch, "E92.0.35", {"start": v(61.5, 24.5) * mm, "end": v(-61.5, 24.5) * mm});
            skLineSegment(sketch, "E93.0", {"start": v(60, 20) * mm, "end": v(63, 20) * mm});
            skLineSegment(sketch, "E93.1", {"start": v(60, 10) * mm, "end": v(63, 10) * mm});
            skLineSegment(sketch, "E93.2", {"start": v(60, 20) * mm, "end": v(60, 10) * mm});
            skLineSegment(sketch, "E93.3", {"start": v(63, 20) * mm, "end": v(63, 10) * mm});
            skLineSegment(sketch, "E93.4", {"start": v(0, 0) * mm, "end": v(0, 17.53) * mm});
            skLineSegment(sketch, "E93.5", {"start": v(0, 0) * mm, "end": v(16.07, 0) * mm});
            skLineSegment(sketch, "E93.6", {"start": v(60, -20) * mm, "end": v(63, -20) * mm});
            skLineSegment(sketch, "E93.7", {"start": v(60, -10) * mm, "end": v(63, -10) * mm});
            skLineSegment(sketch, "E93.8", {"start": v(60, -20) * mm, "end": v(60, -10) * mm});
            skLineSegment(sketch, "E93.9", {"start": v(63, -20) * mm, "end": v(63, -10) * mm});
            skLineSegment(sketch, "E93.10", {"start": v(-60, 10) * mm, "end": v(-63, 10) * mm});
            skLineSegment(sketch, "E93.11", {"start": v(-60, 20) * mm, "end": v(-60, 10) * mm});
            skLineSegment(sketch, "E93.12", {"start": v(-63, 20) * mm, "end": v(-63, 10) * mm});
            skLineSegment(sketch, "E93.13", {"start": v(-60, 20) * mm, "end": v(-63, 20) * mm});
            skLineSegment(sketch, "E93.14", {"start": v(-60, -20) * mm, "end": v(-60, -10) * mm});
            skLineSegment(sketch, "E93.15", {"start": v(-60, -20) * mm, "end": v(-63, -20) * mm});
            skLineSegment(sketch, "E93.16", {"start": v(-63, -20) * mm, "end": v(-63, -10) * mm});
            skLineSegment(sketch, "E93.17", {"start": v(-60, -10) * mm, "end": v(-63, -10) * mm});
            skArc(sketch, "E94.0", {"start": v(-45, 17.5) * mm, "mid": v(-48.54, 16.04) * mm, "end": v(-50, 12.5) * mm});
            skLineSegment(sketch, "E94.1", {"start": v(-45, 17.5) * mm, "end": v(45, 17.5) * mm});
            skLineSegment(sketch, "E94.2", {"start": v(-50, 12.5) * mm, "end": v(-50, -12.5) * mm});
            skArc(sketch, "E94.3", {"start": v(-50, -12.5) * mm, "mid": v(-48.54, -16.04) * mm, "end": v(-45, -17.5) * mm});
            skLineSegment(sketch, "E94.4", {"start": v(-45, -17.5) * mm, "end": v(45, -17.5) * mm});
            skArc(sketch, "E94.5", {"start": v(45, -17.5) * mm, "mid": v(48.54, -16.04) * mm, "end": v(50, -12.5) * mm});
            skLineSegment(sketch, "E94.6", {"start": v(50, 12.5) * mm, "end": v(50, -12.5) * mm});
            skArc(sketch, "E94.7", {"start": v(50, 12.5) * mm, "mid": v(48.54, 16.04) * mm, "end": v(45, 17.5) * mm});
            skSolve(sketch);
        }
        {
            var Q0;
            Q0 = qSketchRegion(id + "F11", true);
            extrude(context, id + "F12", {"entities" : qUnion([Q0]), "depth" : 2 * mm});
        }
        {
            var Q0;
            Q0=makeQuery(id+"F12.opExtrude","CAP_FACE",FACE,{"disambiguationData":[OSD([sQuery(id+"F11.wireOp",EDGE,"E92.0.0"),sQuery(id+"F11.wireOp",EDGE,"E92.0.1"),sQuery(id+"F11.wireOp",EDGE,"E92.0.2"),sQuery(id+"F11.wireOp",EDGE,"E92.0.3"),sQuery(id+"F11.wireOp",EDGE,"E92.0.4"),sQuery(id+"F11.wireOp",EDGE,"E92.0.5"),sQuery(id+"F11.wireOp",EDGE,"E92.0.6"),sQuery(id+"F11.wireOp",EDGE,"E92.0.7"),sQuery(id+"F11.wireOp",EDGE,"E92.0.8"),sQuery(id+"F11.wireOp",EDGE,"E92.0.9"),sQuery(id+"F11.wireOp",EDGE,"E92.0.10"),sQuery(id+"F11.wireOp",EDGE,"E92.0.11"),sQuery(id+"F11.wireOp",EDGE,"E92.0.12"),sQuery(id+"F11.wireOp",EDGE,"E92.0.13"),sQuery(id+"F11.wireOp",EDGE,"E92.0.14"),sQuery(id+"F11.wireOp",EDGE,"E92.0.15"),sQuery(id+"F11.wireOp",EDGE,"E92.0.16"),sQuery(id+"F11.wireOp",EDGE,"E92.0.17"),sQuery(id+"F11.wireOp",EDGE,"E92.0.18"),sQuery(id+"F11.wireOp",EDGE,"E92.0.19"),sQuery(id+"F11.wireOp",EDGE,"E92.0.20"),sQuery(id+"F11.wireOp",EDGE,"E92.0.21"),sQuery(id+"F11.wireOp",EDGE,"E92.0.22"),sQuery(id+"F11.wireOp",EDGE,"E92.0.23"),sQuery(id+"F11.wireOp",EDGE,"E92.0.24"),sQuery(id+"F11.wireOp",EDGE,"E92.0.25"),sQuery(id+"F11.wireOp",EDGE,"E92.0.26"),sQuery(id+"F11.wireOp",EDGE,"E92.0.27"),sQuery(id+"F11.wireOp",EDGE,"E92.0.28"),sQuery(id+"F11.wireOp",EDGE,"E92.0.29"),sQuery(id+"F11.wireOp",EDGE,"E92.0.30"),sQuery(id+"F11.wireOp",EDGE,"E92.0.31"),sQuery(id+"F11.wireOp",EDGE,"E92.0.32"),sQuery(id+"F11.wireOp",EDGE,"E92.0.33"),sQuery(id+"F11.wireOp",EDGE,"E92.0.34"),sQuery(id+"F11.wireOp",EDGE,"E92.0.35"),sQuery(id+"F11.wireOp",EDGE,"E93.0"),sQuery(id+"F11.wireOp",EDGE,"E93.1"),sQuery(id+"F11.wireOp",EDGE,"E93.2"),sQuery(id+"F11.wireOp",EDGE,"E93.3"),sQuery(id+"F11.wireOp",EDGE,"E93.6"),sQuery(id+"F11.wireOp",EDGE,"E93.7"),sQuery(id+"F11.wireOp",EDGE,"E93.8"),sQuery(id+"F11.wireOp",EDGE,"E93.9"),sQuery(id+"F11.wireOp",EDGE,"E93.10"),sQuery(id+"F11.wireOp",EDGE,"E93.11"),sQuery(id+"F11.wireOp",EDGE,"E93.12"),sQuery(id+"F11.wireOp",EDGE,"E93.13"),sQuery(id+"F11.wireOp",EDGE,"E93.14"),sQuery(id+"F11.wireOp",EDGE,"E93.15"),sQuery(id+"F11.wireOp",EDGE,"E93.16"),sQuery(id+"F11.wireOp",EDGE,"E93.17"),sQuery(id+"F11.wireOp",EDGE,"E94.0"),sQuery(id+"F11.wireOp",EDGE,"E94.1"),sQuery(id+"F11.wireOp",EDGE,"E94.2"),sQuery(id+"F11.wireOp",EDGE,"E94.3"),sQuery(id+"F11.wireOp",EDGE,"E94.4"),sQuery(id+"F11.wireOp",EDGE,"E94.5"),sQuery(id+"F11.wireOp",EDGE,"E94.6"),sQuery(id+"F11.wireOp",EDGE,"E94.7")])],"isStart":false});
            var sketch = newSketch(context, id + "F13", { "sketchPlane" : qUnion([Q0])});
            skLineSegment(sketch, "E95.bottom", {"start": v(-84.5, 6.5) * mm, "end": v(-87.5, 6.5) * mm});
            skLineSegment(sketch, "E95.top", {"start": v(-84.5, 3.5) * mm, "end": v(-87.5, 3.5) * mm});
            skLineSegment(sketch, "E95.left", {"start": v(-84.5, 6.5) * mm, "end": v(-84.5, 3.5) * mm});
            skLineSegment(sketch, "E95.right", {"start": v(-87.5, 6.5) * mm, "end": v(-87.5, 3.5) * mm});
            skPoint(sketch, "E95.middle", {"position": v(-86, 5) * mm});
            skLineSegment(sketch, "E96", {"start": v(0, 9.99) * mm, "end": v(0, 0) * mm, "construction": true});
            skLineSegment(sketch, "E97", {"start": v(0, 0) * mm, "end": v(11.58, 0) * mm, "construction": true});
            skLineSegment(sketch, "E98.MirrorCS", {"start": v(87.5, 6.5) * mm, "end": v(87.5, 3.5) * mm});
            skLineSegment(sketch, "E99.MirrorCS", {"start": v(84.5, 6.5) * mm, "end": v(84.5, 3.5) * mm});
            skPoint(sketch, "E100.MirrorP", {"position": v(86, 5) * mm});
            skLineSegment(sketch, "E101.MirrorCS", {"start": v(84.5, 3.5) * mm, "end": v(87.5, 3.5) * mm});
            skLineSegment(sketch, "E102.MirrorCS", {"start": v(84.5, 6.5) * mm, "end": v(87.5, 6.5) * mm});
            skLineSegment(sketch, "E103.MirrorCS", {"start": v(-87.5, -6.5) * mm, "end": v(-87.5, -3.5) * mm});
            skLineSegment(sketch, "E104.MirrorCS", {"start": v(-84.5, -6.5) * mm, "end": v(-84.5, -3.5) * mm});
            skLineSegment(sketch, "E105.MirrorCS", {"start": v(-84.5, -3.5) * mm, "end": v(-87.5, -3.5) * mm});
            skLineSegment(sketch, "E106.MirrorCS", {"start": v(-84.5, -6.5) * mm, "end": v(-87.5, -6.5) * mm});
            skPoint(sketch, "E107.MirrorP", {"position": v(-86, -5) * mm});
            skLineSegment(sketch, "E108.MirrorCS", {"start": v(84.5, -6.5) * mm, "end": v(84.5, -3.5) * mm});
            skLineSegment(sketch, "E109.MirrorCS", {"start": v(87.5, -6.5) * mm, "end": v(87.5, -3.5) * mm});
            skLineSegment(sketch, "E110.MirrorCS", {"start": v(84.5, -3.5) * mm, "end": v(87.5, -3.5) * mm});
            skLineSegment(sketch, "E111.MirrorCS", {"start": v(84.5, -6.5) * mm, "end": v(87.5, -6.5) * mm});
            skPoint(sketch, "E112.MirrorP", {"position": v(86, -5) * mm});
            skCircle(sketch, "E113", {"center": v(-86, 0) * mm, "radius": 1.5 * mm});
            skCircle(sketch, "E114.MirrorC", {"center": v(86, 0) * mm, "radius": 1.5 * mm});
            skSolve(sketch);
        }
        {
            var Q0;
            Q0 = qSketchRegion(id + "F13", true);
            extrude(context, id + "F14", {"entities" : qUnion([Q0]), "operationType" : NewBodyOperationType.REMOVE, "endBound" : BoundingType.THROUGH_ALL, "oppositeDirection" : true, "depth" : 25 * mm});
        }
        {
            var Q0;
            {var subQ0=sQuery(id+"F11.wireOp",EDGE,"E94.7");var subQ1=sQuery(id+"F11.wireOp",EDGE,"E94.6");var subQ2=sQuery(id+"F11.wireOp",EDGE,"E94.5");var subQ3=sQuery(id+"F11.wireOp",EDGE,"E94.4");var subQ4=sQuery(id+"F11.wireOp",EDGE,"E94.3");var subQ5=sQuery(id+"F11.wireOp",EDGE,"E94.2");var subQ6=sQuery(id+"F11.wireOp",EDGE,"E94.1");var subQ7=sQuery(id+"F11.wireOp",EDGE,"E94.0");var subQ8=sQuery(id+"F11.wireOp",EDGE,"E93.17");var subQ9=sQuery(id+"F11.wireOp",EDGE,"E93.16");var subQ10=sQuery(id+"F11.wireOp",EDGE,"E93.15");var subQ11=sQuery(id+"F11.wireOp",EDGE,"E93.14");var subQ12=sQuery(id+"F11.wireOp",EDGE,"E93.13");var subQ13=sQuery(id+"F11.wireOp",EDGE,"E93.12");var subQ14=sQuery(id+"F11.wireOp",EDGE,"E93.11");var subQ15=sQuery(id+"F11.wireOp",EDGE,"E93.10");var subQ16=sQuery(id+"F11.wireOp",EDGE,"E93.9");var subQ17=sQuery(id+"F11.wireOp",EDGE,"E93.8");var subQ18=sQuery(id+"F11.wireOp",EDGE,"E93.7");var subQ19=sQuery(id+"F11.wireOp",EDGE,"E93.6");var subQ20=sQuery(id+"F11.wireOp",EDGE,"E93.3");var subQ21=sQuery(id+"F11.wireOp",EDGE,"E93.2");var subQ22=sQuery(id+"F11.wireOp",EDGE,"E93.1");var subQ23=sQuery(id+"F11.wireOp",EDGE,"E93.0");var subQ24=sQuery(id+"F11.wireOp",EDGE,"E92.0.35");var subQ25=sQuery(id+"F11.wireOp",EDGE,"E92.0.34");var subQ26=sQuery(id+"F11.wireOp",EDGE,"E92.0.33");var subQ27=sQuery(id+"F11.wireOp",EDGE,"E92.0.32");var subQ28=sQuery(id+"F11.wireOp",EDGE,"E92.0.31");var subQ29=sQuery(id+"F11.wireOp",EDGE,"E92.0.30");var subQ30=sQuery(id+"F11.wireOp",EDGE,"E92.0.29");var subQ31=sQuery(id+"F11.wireOp",EDGE,"E92.0.28");var subQ32=sQuery(id+"F11.wireOp",EDGE,"E92.0.27");var subQ33=sQuery(id+"F11.wireOp",EDGE,"E92.0.26");var subQ34=sQuery(id+"F11.wireOp",EDGE,"E92.0.25");var subQ35=sQuery(id+"F11.wireOp",EDGE,"E92.0.24");var subQ36=sQuery(id+"F11.wireOp",EDGE,"E92.0.23");var subQ37=sQuery(id+"F11.wireOp",EDGE,"E92.0.22");var subQ38=sQuery(id+"F11.wireOp",EDGE,"E92.0.21");var subQ39=sQuery(id+"F11.wireOp",EDGE,"E92.0.20");var subQ40=sQuery(id+"F11.wireOp",EDGE,"E92.0.19");var subQ41=sQuery(id+"F11.wireOp",EDGE,"E92.0.18");var subQ42=sQuery(id+"F11.wireOp",EDGE,"E92.0.17");var subQ43=sQuery(id+"F11.wireOp",EDGE,"E92.0.16");var subQ44=sQuery(id+"F11.wireOp",EDGE,"E92.0.15");var subQ45=sQuery(id+"F11.wireOp",EDGE,"E92.0.14");var subQ46=sQuery(id+"F11.wireOp",EDGE,"E92.0.13");var subQ47=sQuery(id+"F11.wireOp",EDGE,"E92.0.12");var subQ48=sQuery(id+"F11.wireOp",EDGE,"E92.0.11");var subQ49=sQuery(id+"F11.wireOp",EDGE,"E92.0.10");var subQ50=sQuery(id+"F11.wireOp",EDGE,"E92.0.9");var subQ51=sQuery(id+"F11.wireOp",EDGE,"E92.0.8");var subQ52=sQuery(id+"F11.wireOp",EDGE,"E92.0.7");var subQ53=sQuery(id+"F11.wireOp",EDGE,"E92.0.6");var subQ54=sQuery(id+"F11.wireOp",EDGE,"E92.0.5");var subQ55=sQuery(id+"F11.wireOp",EDGE,"E92.0.4");var subQ56=sQuery(id+"F11.wireOp",EDGE,"E92.0.3");var subQ57=sQuery(id+"F11.wireOp",EDGE,"E92.0.2");var subQ58=sQuery(id+"F11.wireOp",EDGE,"E92.0.1");var subQ59=sQuery(id+"F11.wireOp",EDGE,"E92.0.0");Q0=makeQuery(id+"F14.boolean.opBoolean","COPY",FACE,{"disambiguationData":[TD([makeQuery(id+"F12.opExtrude","CAP_FACE",FACE,{"disambiguationData":[OSD([subQ59,subQ58,subQ57,subQ56,subQ55,subQ54,subQ53,subQ52,subQ51,subQ50,subQ49,subQ48,subQ47,subQ46,subQ45,subQ44,subQ43,subQ42,subQ41,subQ40,subQ39,subQ38,subQ37,subQ36,subQ35,subQ34,subQ33,subQ32,subQ31,subQ30,subQ29,subQ28,subQ27,subQ26,subQ25,subQ24,subQ23,subQ22,subQ21,subQ20,subQ19,subQ18,subQ17,subQ16,subQ15,subQ14,subQ13,subQ12,subQ11,subQ10,subQ9,subQ8,subQ7,subQ6,subQ5,subQ4,subQ3,subQ2,subQ1,subQ0])],"isStart":true})])],"derivedFrom":makeQuery(id+"F14.opExtrude","SWEPT_FACE",FACE,{"disambiguationData":[OSD([sQuery(id+"F13.wireOp",EDGE,"E95.left")])]})});}
            var sketch = newSketch(context, id + "F15", { "sketchPlane" : qUnion([Q0])});
            skLineSegment(sketch, "E115.bottom", {"start": v(2, 6.5) * mm, "end": v(102, 6.5) * mm});
            skLineSegment(sketch, "E115.top", {"start": v(2, -6.5) * mm, "end": v(102, -6.5) * mm});
            skLineSegment(sketch, "E115.left", {"start": v(2, 6.5) * mm, "end": v(2, -6.5) * mm});
            skLineSegment(sketch, "E115.right", {"start": v(102, 6.5) * mm, "end": v(102, -6.5) * mm});
            skLineSegment(sketch, "E116.bottom", {"start": v(2, 1.65) * mm, "end": v(12, 1.65) * mm});
            skLineSegment(sketch, "E116.top", {"start": v(2, -1.65) * mm, "end": v(12, -1.65) * mm});
            skLineSegment(sketch, "E116.left", {"start": v(2, 1.65) * mm, "end": v(2, -1.65) * mm});
            skLineSegment(sketch, "E116.right", {"start": v(12, 1.65) * mm, "end": v(12, -1.65) * mm});
            skPoint(sketch, "E116.middle", {"position": v(7, 0) * mm});
            skLineSegment(sketch, "E117.bottom", {"start": v(4, 3.5) * mm, "end": v(7, 3.5) * mm});
            skLineSegment(sketch, "E117.top", {"start": v(4, -3.5) * mm, "end": v(7, -3.5) * mm});
            skLineSegment(sketch, "E117.left", {"start": v(4, 3.5) * mm, "end": v(4, -3.5) * mm});
            skLineSegment(sketch, "E117.right", {"start": v(7, 3.5) * mm, "end": v(7, -3.5) * mm});
            skPoint(sketch, "E117.middle", {"position": v(5.5, 0) * mm});
            skLineSegment(sketch, "E118", {"start": v(52, 6.5) * mm, "end": v(52, -6.5) * mm, "construction": true});
            skLineSegment(sketch, "E119.MirrorCS", {"start": v(100, 3.5) * mm, "end": v(97, 3.5) * mm});
            skLineSegment(sketch, "E120.MirrorCS", {"start": v(97, 3.5) * mm, "end": v(97, -3.5) * mm});
            skLineSegment(sketch, "E121.MirrorCS", {"start": v(102, 1.65) * mm, "end": v(92, 1.65) * mm});
            skLineSegment(sketch, "E122.MirrorCS", {"start": v(92, 1.65) * mm, "end": v(92, -1.65) * mm});
            skLineSegment(sketch, "E123.MirrorCS", {"start": v(102, -1.65) * mm, "end": v(92, -1.65) * mm});
            skLineSegment(sketch, "E124.MirrorCS", {"start": v(100, -3.5) * mm, "end": v(97, -3.5) * mm});
            skLineSegment(sketch, "E125.MirrorCS", {"start": v(100, 3.5) * mm, "end": v(100, -3.5) * mm});
            skSolve(sketch);
        }
        {
            var Q0;
            {var subQ9=sQuery(id+"F15.wireOp",EDGE,"E115.bottom");Q0=makeQuery(id+"F15.imprint","IMPRINT",FACE,{"disambiguationData":[TD([[makeQuery(id+"F15.imprint","IMPRINT",EDGE,{"derivedFrom":subQ9}),-1.0]])]});}
            var Q1;
            {var subQ0=sQuery(id+"F0.wireOp",EDGE,"E34.MirrorCS");var subQ1=sQuery(id+"F0.wireOp",EDGE,"E33.MirrorCS");var subQ2=sQuery(id+"F0.wireOp",EDGE,"E32.MirrorCS");var subQ3=sQuery(id+"F0.wireOp",EDGE,"E31.MirrorCS");var subQ4=sQuery(id+"F0.wireOp",EDGE,"E30.right");var subQ5=sQuery(id+"F0.wireOp",EDGE,"E30.left");var subQ6=sQuery(id+"F0.wireOp",EDGE,"E30.top");var subQ7=sQuery(id+"F0.wireOp",EDGE,"E30.bottom");var subQ8=sQuery(id+"F0.wireOp",EDGE,"E29");var subQ9=sQuery(id+"F0.wireOp",EDGE,"E27.MirrorCS");var subQ10=sQuery(id+"F0.wireOp",EDGE,"E26.MirrorCS");var subQ11=sQuery(id+"F0.wireOp",EDGE,"E25");var subQ12=sQuery(id+"F0.wireOp",EDGE,"E24");var subQ13=sQuery(id+"F0.wireOp",EDGE,"E23");var subQ14=sQuery(id+"F0.wireOp",EDGE,"E22.MirrorC");var subQ15=sQuery(id+"F0.wireOp",EDGE,"E21");var subQ16=sQuery(id+"F0.wireOp",EDGE,"E20.MirrorCS");var subQ17=sQuery(id+"F0.wireOp",EDGE,"E19.MirrorC");var subQ18=sQuery(id+"F0.wireOp",EDGE,"E18.MirrorCS");var subQ19=sQuery(id+"F0.wireOp",EDGE,"E17.MirrorCS");var subQ20=sQuery(id+"F0.wireOp",EDGE,"E16.MirrorC");var subQ21=sQuery(id+"F0.wireOp",EDGE,"E15.MirrorCS");var subQ22=sQuery(id+"F0.wireOp",EDGE,"E14.MirrorCS");var subQ23=sQuery(id+"F0.wireOp",EDGE,"E13.MirrorCS");var subQ24=sQuery(id+"F0.wireOp",EDGE,"E12.MirrorC");var subQ25=sQuery(id+"F0.wireOp",EDGE,"E9");var subQ26=sQuery(id+"F0.wireOp",EDGE,"E8");var subQ27=sQuery(id+"F0.wireOp",EDGE,"E5");var subQ28=sQuery(id+"F0.wireOp",EDGE,"E4.2");var subQ29=sQuery(id+"F0.wireOp",EDGE,"E4.0");Q1=makeQuery(id+"F14.boolean.opBoolean","COPY",FACE,{"disambiguationData":[TD([makeQuery(id+"F1.opExtrude","CAP_FACE",FACE,{"disambiguationData":[OSD([subQ29,subQ28,subQ27,subQ26,subQ25,subQ24,subQ23,subQ22,subQ21,subQ20,subQ19,subQ18,subQ17,subQ16,subQ15,subQ14,subQ13,subQ12,subQ11,subQ10,subQ9,subQ8,subQ7,subQ6,subQ5,subQ4,subQ3,subQ2,subQ1,subQ0])],"isStart":true})])],"derivedFrom":makeQuery(id+"F14.opExtrude","SWEPT_FACE",FACE,{"disambiguationData":[OSD([sQuery(id+"F13.wireOp",EDGE,"E95.left")])]})});}
            var Q2;
            {var subQ0=sQuery(id+"F0.wireOp",EDGE,"E34.MirrorCS");var subQ1=sQuery(id+"F0.wireOp",EDGE,"E33.MirrorCS");var subQ2=sQuery(id+"F0.wireOp",EDGE,"E32.MirrorCS");var subQ3=sQuery(id+"F0.wireOp",EDGE,"E31.MirrorCS");var subQ4=sQuery(id+"F0.wireOp",EDGE,"E30.right");var subQ5=sQuery(id+"F0.wireOp",EDGE,"E30.left");var subQ6=sQuery(id+"F0.wireOp",EDGE,"E30.top");var subQ7=sQuery(id+"F0.wireOp",EDGE,"E30.bottom");var subQ8=sQuery(id+"F0.wireOp",EDGE,"E29");var subQ9=sQuery(id+"F0.wireOp",EDGE,"E27.MirrorCS");var subQ10=sQuery(id+"F0.wireOp",EDGE,"E26.MirrorCS");var subQ11=sQuery(id+"F0.wireOp",EDGE,"E25");var subQ12=sQuery(id+"F0.wireOp",EDGE,"E24");var subQ13=sQuery(id+"F0.wireOp",EDGE,"E23");var subQ14=sQuery(id+"F0.wireOp",EDGE,"E22.MirrorC");var subQ15=sQuery(id+"F0.wireOp",EDGE,"E21");var subQ16=sQuery(id+"F0.wireOp",EDGE,"E20.MirrorCS");var subQ17=sQuery(id+"F0.wireOp",EDGE,"E19.MirrorC");var subQ18=sQuery(id+"F0.wireOp",EDGE,"E18.MirrorCS");var subQ19=sQuery(id+"F0.wireOp",EDGE,"E17.MirrorCS");var subQ20=sQuery(id+"F0.wireOp",EDGE,"E16.MirrorC");var subQ21=sQuery(id+"F0.wireOp",EDGE,"E15.MirrorCS");var subQ22=sQuery(id+"F0.wireOp",EDGE,"E14.MirrorCS");var subQ23=sQuery(id+"F0.wireOp",EDGE,"E13.MirrorCS");var subQ24=sQuery(id+"F0.wireOp",EDGE,"E12.MirrorC");var subQ25=sQuery(id+"F0.wireOp",EDGE,"E9");var subQ26=sQuery(id+"F0.wireOp",EDGE,"E8");var subQ27=sQuery(id+"F0.wireOp",EDGE,"E5");var subQ28=sQuery(id+"F0.wireOp",EDGE,"E4.2");var subQ29=sQuery(id+"F0.wireOp",EDGE,"E4.0");Q2=makeQuery(id+"F14.boolean.opBoolean","COPY",FACE,{"disambiguationData":[TD([makeQuery(id+"F1.opExtrude","CAP_FACE",FACE,{"disambiguationData":[OSD([subQ29,subQ28,subQ27,subQ26,subQ25,subQ24,subQ23,subQ22,subQ21,subQ20,subQ19,subQ18,subQ17,subQ16,subQ15,subQ14,subQ13,subQ12,subQ11,subQ10,subQ9,subQ8,subQ7,subQ6,subQ5,subQ4,subQ3,subQ2,subQ1,subQ0])],"isStart":true})])],"derivedFrom":makeQuery(id+"F14.opExtrude","SWEPT_FACE",FACE,{"disambiguationData":[OSD([sQuery(id+"F13.wireOp",EDGE,"E104.MirrorCS")])]})});}
            var Q3;
            {var subQ64=sQuery(id+"F13.wireOp",EDGE,"E95.left");Q3=makeQuery(id+"F15.imprint","IMPRINT",FACE,{"disambiguationData":[TD([[makeQuery(id+"F15.imprint","IMPRINT",EDGE,{"derivedFrom":makeQuery(id+"F14.boolean.opBoolean","COPY",EDGE,{"derivedFrom":makeQuery(id+"F14.opExtrude","CAP_EDGE",EDGE,{"disambiguationData":[OSD([subQ64])],"isStart":true})})}),-1.0]])]});}
            var Q4;
            {var subQ0=sQuery(id+"F11.wireOp",EDGE,"E94.7");var subQ1=sQuery(id+"F11.wireOp",EDGE,"E94.6");var subQ2=sQuery(id+"F11.wireOp",EDGE,"E94.5");var subQ3=sQuery(id+"F11.wireOp",EDGE,"E94.4");var subQ4=sQuery(id+"F11.wireOp",EDGE,"E94.3");var subQ5=sQuery(id+"F11.wireOp",EDGE,"E94.2");var subQ6=sQuery(id+"F11.wireOp",EDGE,"E94.1");var subQ7=sQuery(id+"F11.wireOp",EDGE,"E94.0");var subQ8=sQuery(id+"F11.wireOp",EDGE,"E93.17");var subQ9=sQuery(id+"F11.wireOp",EDGE,"E93.16");var subQ10=sQuery(id+"F11.wireOp",EDGE,"E93.15");var subQ11=sQuery(id+"F11.wireOp",EDGE,"E93.14");var subQ12=sQuery(id+"F11.wireOp",EDGE,"E93.13");var subQ13=sQuery(id+"F11.wireOp",EDGE,"E93.12");var subQ14=sQuery(id+"F11.wireOp",EDGE,"E93.11");var subQ15=sQuery(id+"F11.wireOp",EDGE,"E93.10");var subQ16=sQuery(id+"F11.wireOp",EDGE,"E93.9");var subQ17=sQuery(id+"F11.wireOp",EDGE,"E93.8");var subQ18=sQuery(id+"F11.wireOp",EDGE,"E93.7");var subQ19=sQuery(id+"F11.wireOp",EDGE,"E93.6");var subQ20=sQuery(id+"F11.wireOp",EDGE,"E93.3");var subQ21=sQuery(id+"F11.wireOp",EDGE,"E93.2");var subQ22=sQuery(id+"F11.wireOp",EDGE,"E93.1");var subQ23=sQuery(id+"F11.wireOp",EDGE,"E93.0");var subQ24=sQuery(id+"F11.wireOp",EDGE,"E92.0.35");var subQ25=sQuery(id+"F11.wireOp",EDGE,"E92.0.34");var subQ26=sQuery(id+"F11.wireOp",EDGE,"E92.0.33");var subQ27=sQuery(id+"F11.wireOp",EDGE,"E92.0.32");var subQ28=sQuery(id+"F11.wireOp",EDGE,"E92.0.31");var subQ29=sQuery(id+"F11.wireOp",EDGE,"E92.0.30");var subQ30=sQuery(id+"F11.wireOp",EDGE,"E92.0.29");var subQ31=sQuery(id+"F11.wireOp",EDGE,"E92.0.28");var subQ32=sQuery(id+"F11.wireOp",EDGE,"E92.0.27");var subQ33=sQuery(id+"F11.wireOp",EDGE,"E92.0.26");var subQ34=sQuery(id+"F11.wireOp",EDGE,"E92.0.25");var subQ35=sQuery(id+"F11.wireOp",EDGE,"E92.0.24");var subQ36=sQuery(id+"F11.wireOp",EDGE,"E92.0.23");var subQ37=sQuery(id+"F11.wireOp",EDGE,"E92.0.22");var subQ38=sQuery(id+"F11.wireOp",EDGE,"E92.0.21");var subQ39=sQuery(id+"F11.wireOp",EDGE,"E92.0.20");var subQ40=sQuery(id+"F11.wireOp",EDGE,"E92.0.19");var subQ41=sQuery(id+"F11.wireOp",EDGE,"E92.0.18");var subQ42=sQuery(id+"F11.wireOp",EDGE,"E92.0.17");var subQ43=sQuery(id+"F11.wireOp",EDGE,"E92.0.16");var subQ44=sQuery(id+"F11.wireOp",EDGE,"E92.0.15");var subQ45=sQuery(id+"F11.wireOp",EDGE,"E92.0.14");var subQ46=sQuery(id+"F11.wireOp",EDGE,"E92.0.13");var subQ47=sQuery(id+"F11.wireOp",EDGE,"E92.0.12");var subQ48=sQuery(id+"F11.wireOp",EDGE,"E92.0.11");var subQ49=sQuery(id+"F11.wireOp",EDGE,"E92.0.10");var subQ50=sQuery(id+"F11.wireOp",EDGE,"E92.0.9");var subQ51=sQuery(id+"F11.wireOp",EDGE,"E92.0.8");var subQ52=sQuery(id+"F11.wireOp",EDGE,"E92.0.7");var subQ53=sQuery(id+"F11.wireOp",EDGE,"E92.0.6");var subQ54=sQuery(id+"F11.wireOp",EDGE,"E92.0.5");var subQ55=sQuery(id+"F11.wireOp",EDGE,"E92.0.4");var subQ56=sQuery(id+"F11.wireOp",EDGE,"E92.0.3");var subQ57=sQuery(id+"F11.wireOp",EDGE,"E92.0.2");var subQ58=sQuery(id+"F11.wireOp",EDGE,"E92.0.1");var subQ59=sQuery(id+"F11.wireOp",EDGE,"E92.0.0");Q4=makeQuery(id+"F14.boolean.opBoolean","COPY",FACE,{"disambiguationData":[TD([makeQuery(id+"F12.opExtrude","CAP_FACE",FACE,{"disambiguationData":[OSD([subQ59,subQ58,subQ57,subQ56,subQ55,subQ54,subQ53,subQ52,subQ51,subQ50,subQ49,subQ48,subQ47,subQ46,subQ45,subQ44,subQ43,subQ42,subQ41,subQ40,subQ39,subQ38,subQ37,subQ36,subQ35,subQ34,subQ33,subQ32,subQ31,subQ30,subQ29,subQ28,subQ27,subQ26,subQ25,subQ24,subQ23,subQ22,subQ21,subQ20,subQ19,subQ18,subQ17,subQ16,subQ15,subQ14,subQ13,subQ12,subQ11,subQ10,subQ9,subQ8,subQ7,subQ6,subQ5,subQ4,subQ3,subQ2,subQ1,subQ0])],"isStart":true})])],"derivedFrom":makeQuery(id+"F14.opExtrude","SWEPT_FACE",FACE,{"disambiguationData":[OSD([sQuery(id+"F13.wireOp",EDGE,"E104.MirrorCS")])]})});}
            extrude(context, id + "F16", {"entities" : qUnion([Q0, Q1, Q2, Q3, Q4]), "depth" : 3 * mm});
        }
        {
            var Q0;
            Q0=makeQuery(id+"F16.opExtrude","SWEPT_FACE",FACE,{"disambiguationData":[OSD([sQuery(id+"F13.wireOp",EDGE,"E95.left")])]});
            var sketch = newSketch(context, id + "F17", { "sketchPlane" : qUnion([Q0])});
            skLineSegment(sketch, "E126.1.0", {"start": v(-84.5, -6.5) * mm, "end": v(-84.5, -3.5) * mm});
            skLineSegment(sketch, "E126.1.1", {"start": v(-84.5, -3.5) * mm, "end": v(-87.5, -3.5) * mm});
            skLineSegment(sketch, "E126.1.2", {"start": v(-87.5, -3.5) * mm, "end": v(-87.5, -6.5) * mm});
            skLineSegment(sketch, "E126.1.3", {"start": v(-87.5, -6.5) * mm, "end": v(-84.5, -6.5) * mm});
            skLineSegment(sketch, "E127.bottom", {"start": v(-87.5, 6.5) * mm, "end": v(-84.5, 6.5) * mm});
            skLineSegment(sketch, "E127.top", {"start": v(-87.5, 3.5) * mm, "end": v(-84.5, 3.5) * mm});
            skLineSegment(sketch, "E127.left", {"start": v(-87.5, 6.5) * mm, "end": v(-87.5, 3.5) * mm});
            skLineSegment(sketch, "E127.right", {"start": v(-84.5, 6.5) * mm, "end": v(-84.5, 3.5) * mm});
            skSolve(sketch);
        }
        {
            var Q0;
            Q0 = qSketchRegion(id + "F17", true);
            extrude(context, id + "F18", {"entities" : qUnion([Q0]), "operationType" : NewBodyOperationType.ADD, "depth" : 7 * mm});
        }
    });
